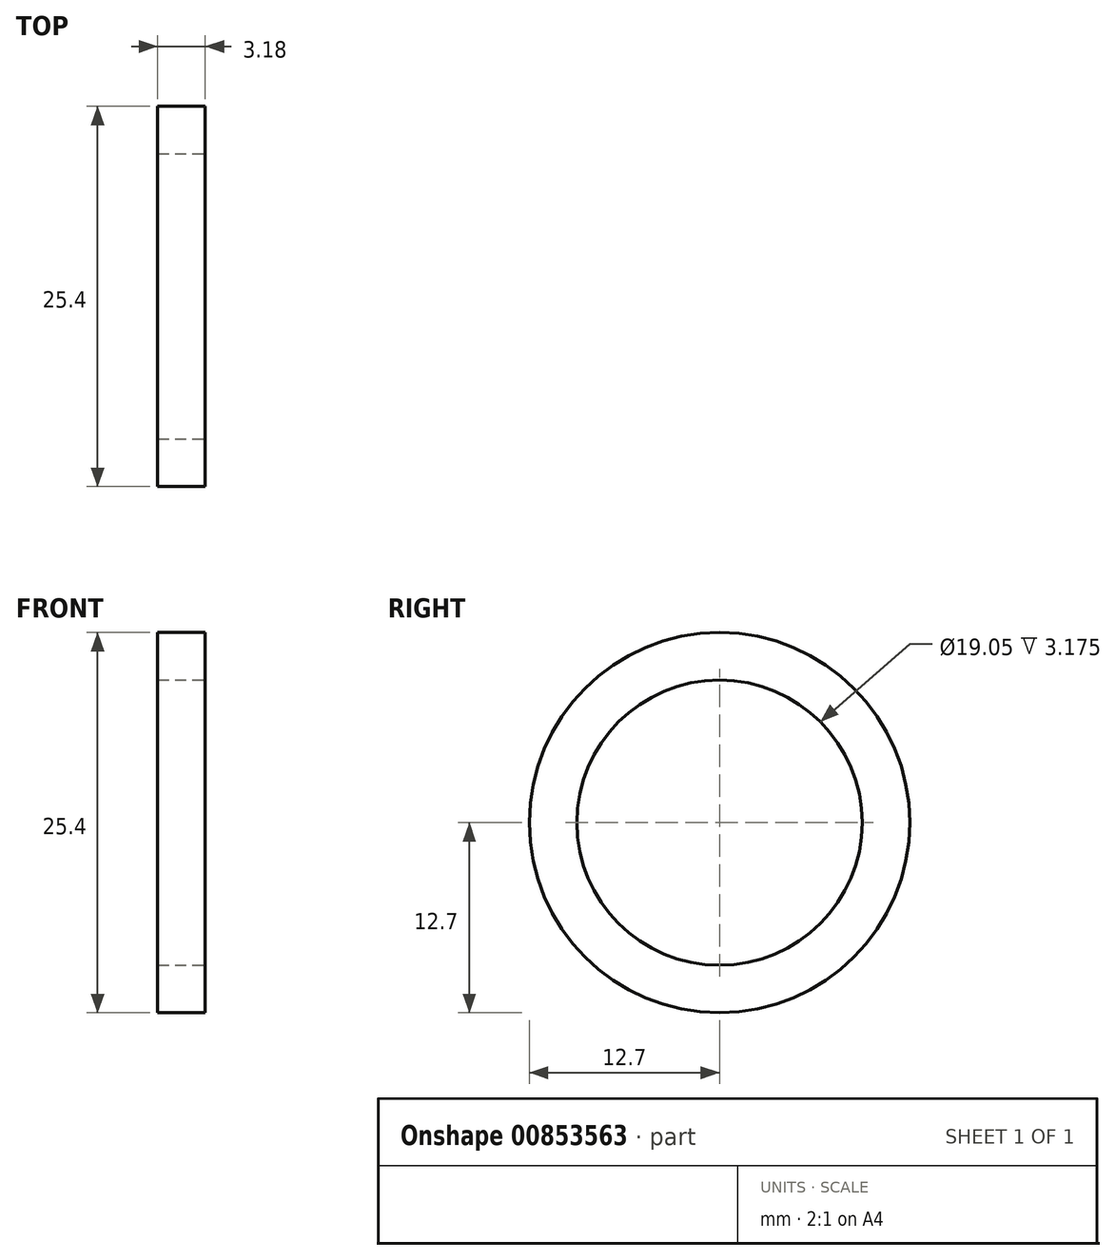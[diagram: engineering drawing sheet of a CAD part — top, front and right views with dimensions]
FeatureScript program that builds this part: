
annotation { "Feature Type Name" : "Feature", "Feature Type Description" : "" }
export const myFeature = defineFeature(function(context is Context, id is Id, definition is map)
    precondition{}
    {
        {
            var Q0;
            Q0=qCreatedBy(makeId("Right.planeOp"),FACE);
            var sketch = newSketch(context, id + "F0", { "sketchPlane" : qUnion([Q0])});
            skCircle(sketch, "E0", {"center": v(0, -0.72) * mm, "radius": 12.7 * mm});
            skCircle(sketch, "E1", {"center": v(0, -0.72) * mm, "radius": 9.53 * mm});
            skSolve(sketch);
        }
        {
            var Q0;
            Q0 = qSketchRegion(id + "F0", true);
            extrude(context, id + "F1", {"entities" : qUnion([Q0]), "oppositeDirection" : true, "depth" : 3.17 * mm, "offsetDistance" : 25.4 * mm});
        }
    });
